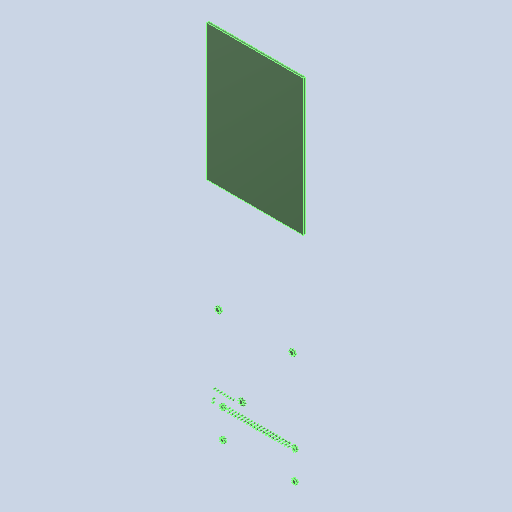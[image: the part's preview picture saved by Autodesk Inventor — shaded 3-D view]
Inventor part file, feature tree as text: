
AUTODESK INVENTOR PART (.ipt)
format: ipt  version: 2022 (Build 260153000, 153)  size: 270,848 bytes
history: native  units: in
note: dims shown in document units (in); Inventor stores cm internally (conversion verified against a paired STEP export)
features: extrude x1, sketch x1
ambient origin geometry x8: Origin, YZ Plane, XZ Plane, XY Plane, X Axis, Y Axis, Z Axis, Center Point
bodies: Solid1 (feature_tree)
feature tree (2):
  extrude  "KiCad-OBC.kicad_pcb_Outline"  [1 undecoded]
  sketch  "Sketch1"  dims[d0=0.063in d1=0.0in]
note: 1 required parameter value undecoded (feature->parameter linkage not recoverable at this tier; creation-order binding heuristic only, values carry confidence <= 0.55)
